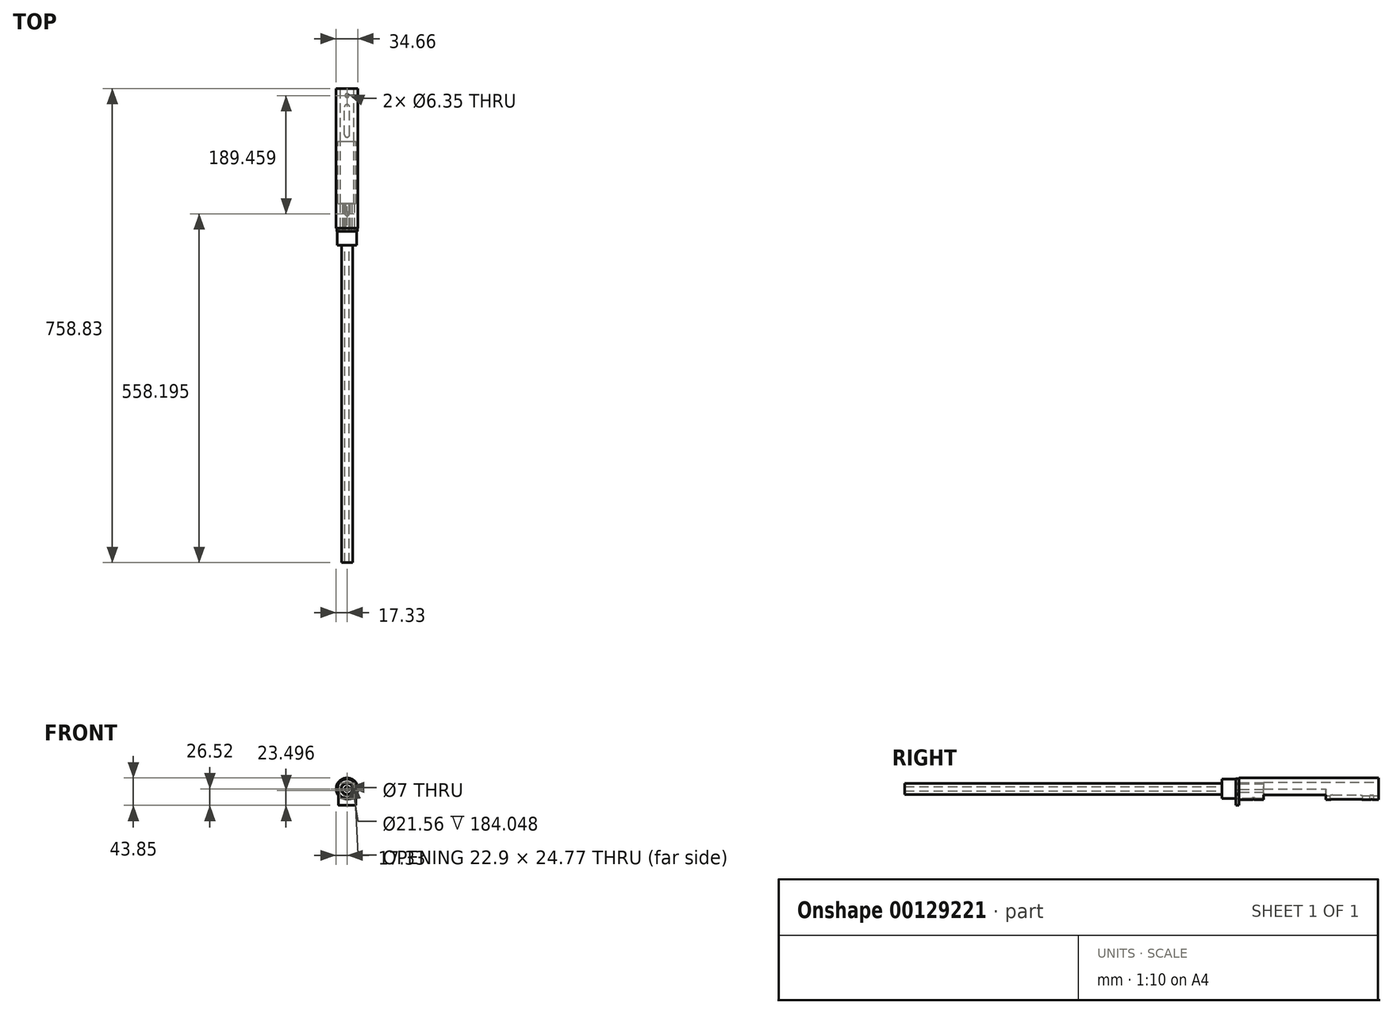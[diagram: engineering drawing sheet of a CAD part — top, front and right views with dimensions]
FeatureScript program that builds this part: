
annotation { "Feature Type Name" : "Feature", "Feature Type Description" : "" }
export const myFeature = defineFeature(function(context is Context, id is Id, definition is map)
    precondition{}
    {
        {
            var Q0;
            Q0=qCreatedBy(makeId("Front.planeOp"),FACE);
            var sketch = newSketch(context, id + "F0", { "sketchPlane" : qUnion([Q0])});
            skCircle(sketch, "E0", {"center": v(0, 0) * mm, "radius": 17.33 * mm});
            skCircle(sketch, "E1.0", {"center": v(0, 0) * mm, "radius": 10.78 * mm});
            skSolve(sketch);
        }
        {
            var Q0;
            Q0 = qSketchRegion(id + "F0", true);
            extrude(context, id + "F1", {"entities" : qUnion([Q0]), "depth" : 184.05 * mm, "offsetDistance" : 25.4 * mm});
        }
        {
            var Q0;
            Q0=makeQuery(id+"F1.opExtrude","CAP_FACE",FACE,{"disambiguationData":[OSD([sQuery(id+"F0.wireOp",EDGE,"E0"),sQuery(id+"F0.wireOp",EDGE,"E1.0")])],"isStart":false});
            var sketch = newSketch(context, id + "F2", { "sketchPlane" : qUnion([Q0])});
            skCircle(sketch, "E2.0", {"center": v(0, 0) * mm, "radius": 17.33 * mm});
            skSolve(sketch);
        }
        {
            var Q0;
            Q0 = qSketchRegion(id + "F2", true);
            extrude(context, id + "F3", {"entities" : qUnion([Q0]), "operationType" : NewBodyOperationType.ADD, "depth" : 39.5 * mm, "offsetDistance" : 25.4 * mm});
        }
        {
            var Q0;
            Q0=makeQuery(id+"F3.opExtrude","CAP_FACE",FACE,{"disambiguationData":[OSD([sQuery(id+"F2.wireOp",EDGE,"E2.0")])],"isStart":false});
            var sketch = newSketch(context, id + "F4", { "sketchPlane" : qUnion([Q0])});
            skArc(sketch, "E3", {"start": v(2.66, 7.14) * mm, "mid": v(0, 7.62) * mm, "end": v(-2.66, 7.14) * mm});
            skLineSegment(sketch, "E4", {"start": v(2.66, 7.14) * mm, "end": v(6.43, 9.32) * mm});
            skLineSegment(sketch, "E5", {"start": v(6.87, 9.2) * mm, "end": v(11.4, 1.35) * mm});
            skLineSegment(sketch, "E6", {"start": v(11.29, 0.9) * mm, "end": v(7.51, -1.27) * mm});
            skLineSegment(sketch, "E7.1.0", {"start": v(-6.43, 9.32) * mm, "end": v(-2.66, 7.14) * mm});
            skLineSegment(sketch, "E7.1.1", {"start": v(-11.4, 1.35) * mm, "end": v(-6.87, 9.2) * mm});
            skLineSegment(sketch, "E7.1.2", {"start": v(-7.51, -1.27) * mm, "end": v(-11.29, 0.9) * mm});
            skLineSegment(sketch, "E7.2.0", {"start": v(-4.86, -10.55) * mm, "end": v(-4.86, -5.87) * mm});
            skLineSegment(sketch, "E7.2.1", {"start": v(4.86, -10.55) * mm, "end": v(-4.86, -10.55) * mm, "construction": true});
            skLineSegment(sketch, "E7.2.2", {"start": v(4.86, -5.87) * mm, "end": v(4.86, -10.55) * mm});
            skPoint(sketch, "E8", {"position": v(0, -10.55) * mm});
            skArc(sketch, "E9", {"start": v(-4.86, -10.55) * mm, "mid": v(0, -15.41) * mm, "end": v(4.86, -10.55) * mm});
            skArc(sketch, "E10.trimOffspring", {"start": v(4.86, -5.87) * mm, "mid": v(6.6, -3.8) * mm, "end": v(7.51, -1.27) * mm});
            skArc(sketch, "E11.trimOffspring", {"start": v(-7.51, -1.27) * mm, "mid": v(-6.6, -3.8) * mm, "end": v(-4.86, -5.87) * mm});
            skPoint(sketch, "E12.visualSharp", {"position": v(11.57, 1.07) * mm});
            skArc(sketch, "E12.filletArc", {"start": v(11.29, 0.9) * mm, "mid": v(11.44, 1.1) * mm, "end": v(11.4, 1.35) * mm});
            skPoint(sketch, "E13.visualSharp", {"position": v(6.71, 9.48) * mm});
            skArc(sketch, "E13.filletArc", {"start": v(6.87, 9.2) * mm, "mid": v(6.68, 9.35) * mm, "end": v(6.43, 9.32) * mm});
            skPoint(sketch, "E14.visualSharp", {"position": v(-6.71, 9.48) * mm});
            skArc(sketch, "E14.filletArc", {"start": v(-6.43, 9.32) * mm, "mid": v(-6.68, 9.35) * mm, "end": v(-6.87, 9.2) * mm});
            skPoint(sketch, "E15.visualSharp", {"position": v(-11.57, 1.07) * mm});
            skArc(sketch, "E15.filletArc", {"start": v(-11.4, 1.35) * mm, "mid": v(-11.44, 1.1) * mm, "end": v(-11.29, 0.9) * mm});
            skSolve(sketch);
        }
        {
            var Q0;
            Q0 = qSketchRegion(id + "F4", true);
            var Q1;
            Q1=makeQuery(id+"F3.opExtrude","CAP_FACE",FACE,{"disambiguationData":[OSD([sQuery(id+"F2.wireOp",EDGE,"E2.0")])],"isStart":true});
            extrude(context, id + "F5", {"entities" : qUnion([Q0]), "operationType" : NewBodyOperationType.REMOVE, "endBound" : BoundingType.UP_TO_SURFACE, "oppositeDirection" : true, "depth" : 25.4 * mm, "endBoundEntityFace" : qUnion([Q1]), "offsetDistance" : 25.4 * mm});
        }
        {
            var Q0;
            Q0=makeQuery(id+"F3.opExtrude","CAP_FACE",FACE,{"disambiguationData":[OSD([sQuery(id+"F2.wireOp",EDGE,"E2.0")])],"isStart":false});
            var sketch = newSketch(context, id + "F6", { "sketchPlane" : qUnion([Q0])});
            skArc(sketch, "E16", {"start": v(13.92, -8.94) * mm, "mid": v(0, 16.54) * mm, "end": v(-13.92, -8.94) * mm});
            skLineSegment(sketch, "E17", {"start": v(-13.92, -8.94) * mm, "end": v(-13.92, -25.74) * mm});
            skLineSegment(sketch, "E18", {"start": v(-13.13, -26.52) * mm, "end": v(13.13, -26.52) * mm});
            skLineSegment(sketch, "E19", {"start": v(13.92, -25.74) * mm, "end": v(13.92, -8.94) * mm});
            skPoint(sketch, "E20", {"position": v(0, -26.52) * mm});
            skPoint(sketch, "E21.visualSharp", {"position": v(-13.92, -26.52) * mm});
            skArc(sketch, "E21.filletArc", {"start": v(-13.92, -25.74) * mm, "mid": v(-13.69, -26.3) * mm, "end": v(-13.13, -26.52) * mm});
            skPoint(sketch, "E22.visualSharp", {"position": v(13.92, -26.52) * mm});
            skArc(sketch, "E22.filletArc", {"start": v(13.13, -26.52) * mm, "mid": v(13.69, -26.3) * mm, "end": v(13.92, -25.74) * mm});
            skArc(sketch, "E23", {"start": v(-7.51, -1.27) * mm, "mid": v(-6.6, -3.8) * mm, "end": v(-4.86, -5.87) * mm});
            skLineSegment(sketch, "E24", {"start": v(-7.51, -1.27) * mm, "end": v(-11.29, 0.9) * mm});
            skArc(sketch, "E25", {"start": v(-11.4, 1.35) * mm, "mid": v(-11.44, 1.1) * mm, "end": v(-11.29, 0.9) * mm});
            skLineSegment(sketch, "E26", {"start": v(-11.4, 1.35) * mm, "end": v(-6.87, 9.2) * mm});
            skArc(sketch, "E27", {"start": v(-6.43, 9.32) * mm, "mid": v(-6.68, 9.35) * mm, "end": v(-6.87, 9.2) * mm});
            skLineSegment(sketch, "E28", {"start": v(-6.43, 9.32) * mm, "end": v(-2.66, 7.14) * mm});
            skArc(sketch, "E29", {"start": v(2.66, 7.14) * mm, "mid": v(0, 7.62) * mm, "end": v(-2.66, 7.14) * mm});
            skLineSegment(sketch, "E30", {"start": v(2.66, 7.14) * mm, "end": v(6.43, 9.32) * mm});
            skArc(sketch, "E31", {"start": v(6.87, 9.2) * mm, "mid": v(6.68, 9.35) * mm, "end": v(6.43, 9.32) * mm});
            skLineSegment(sketch, "E32", {"start": v(6.87, 9.2) * mm, "end": v(11.4, 1.35) * mm});
            skArc(sketch, "E33", {"start": v(11.29, 0.9) * mm, "mid": v(11.44, 1.1) * mm, "end": v(11.4, 1.35) * mm});
            skLineSegment(sketch, "E34", {"start": v(11.29, 0.9) * mm, "end": v(7.51, -1.27) * mm});
            skArc(sketch, "E35", {"start": v(4.86, -5.87) * mm, "mid": v(6.6, -3.8) * mm, "end": v(7.51, -1.27) * mm});
            skLineSegment(sketch, "E36", {"start": v(4.86, -5.87) * mm, "end": v(4.86, -10.55) * mm});
            skArc(sketch, "E37", {"start": v(-4.86, -10.55) * mm, "mid": v(0, -15.41) * mm, "end": v(4.86, -10.55) * mm});
            skLineSegment(sketch, "E38", {"start": v(-4.86, -10.55) * mm, "end": v(-4.86, -5.87) * mm});
            skSolve(sketch);
        }
        {
            var Q0;
            Q0 = qSketchRegion(id + "F6", true);
            extrude(context, id + "F7", {"entities" : qUnion([Q0]), "depth" : 4.97 * mm, "offsetDistance" : 25.4 * mm});
        }
        {
            var Q0;
            Q0=makeQuery(id+"F7.opExtrude","CAP_FACE",FACE,{"disambiguationData":[OSD([sQuery(id+"F6.wireOp",EDGE,"E16"),sQuery(id+"F6.wireOp",EDGE,"E17"),sQuery(id+"F6.wireOp",EDGE,"E18"),sQuery(id+"F6.wireOp",EDGE,"E19"),sQuery(id+"F6.wireOp",EDGE,"E21.filletArc"),sQuery(id+"F6.wireOp",EDGE,"E22.filletArc"),sQuery(id+"F6.wireOp",EDGE,"E23"),sQuery(id+"F6.wireOp",EDGE,"E24"),sQuery(id+"F6.wireOp",EDGE,"E25"),sQuery(id+"F6.wireOp",EDGE,"E26"),sQuery(id+"F6.wireOp",EDGE,"E27"),sQuery(id+"F6.wireOp",EDGE,"E28"),sQuery(id+"F6.wireOp",EDGE,"E29"),sQuery(id+"F6.wireOp",EDGE,"E30"),sQuery(id+"F6.wireOp",EDGE,"E31"),sQuery(id+"F6.wireOp",EDGE,"E32"),sQuery(id+"F6.wireOp",EDGE,"E33"),sQuery(id+"F6.wireOp",EDGE,"E34"),sQuery(id+"F6.wireOp",EDGE,"E35"),sQuery(id+"F6.wireOp",EDGE,"E36"),sQuery(id+"F6.wireOp",EDGE,"E37"),sQuery(id+"F6.wireOp",EDGE,"E38")])],"isStart":false});
            var sketch = newSketch(context, id + "F8", { "sketchPlane" : qUnion([Q0])});
            skCircle(sketch, "E39", {"center": v(0, 0) * mm, "radius": 15.41 * mm});
            skSolve(sketch);
        }
        {
            var Q0;
            Q0 = qSketchRegion(id + "F8", true);
            extrude(context, id + "F9", {"entities" : qUnion([Q0]), "depth" : 22.3 * mm, "offsetDistance" : 25.4 * mm});
        }
        {
            var Q0;
            Q0=makeQuery(id+"F9.opExtrude","CAP_FACE",FACE,{"disambiguationData":[OSD([sQuery(id+"F8.wireOp",EDGE,"E39")])],"isStart":false});
            var sketch = newSketch(context, id + "F10", { "sketchPlane" : qUnion([Q0])});
            skCircle(sketch, "E40", {"center": v(0, 0) * mm, "radius": 8.9 * mm});
            skCircle(sketch, "E41", {"center": v(0, 0) * mm, "radius": 3.5 * mm});
            skSolve(sketch);
        }
        {
            var Q0;
            Q0=makeQuery(id+"F10.imprint","IMPRINT",FACE,{"disambiguationData":[TD([[makeQuery(id+"F10.imprint","IMPRINT",EDGE,{"derivedFrom":sQuery(id+"F10.wireOp",EDGE,"E40")}),1.0]])]});
            var Q1;
            Q1=sQuery(id+"F10.wireOp",EDGE,"E40");
            extrude(context, id + "F11", {"entities" : qUnion([Q0]), "surfaceEntities" : qUnion([Q1]), "depth" : 508 * mm, "offsetDistance" : 25.4 * mm});
        }
        {
            var Q0;
            Q0=qCreatedBy(makeId("Top.planeOp"),FACE);
            var sketch = newSketch(context, id + "F12", { "sketchPlane" : qUnion([Q0])});
            skLineSegment(sketch, "E42.bottom", {"start": v(-14.26, -184.12) * mm, "end": v(14.26, -184.12) * mm});
            skLineSegment(sketch, "E42.top", {"start": v(-14.26, -84.7) * mm, "end": v(14.26, -84.7) * mm});
            skLineSegment(sketch, "E42.left", {"start": v(-14.26, -184.12) * mm, "end": v(-14.26, -84.7) * mm});
            skLineSegment(sketch, "E42.right", {"start": v(14.26, -184.12) * mm, "end": v(14.26, -84.7) * mm});
            skPoint(sketch, "E43", {"position": v(0, -84.7) * mm});
            skSolve(sketch);
        }
        {
            var Q0;
            Q0 = qSketchRegion(id + "F12", true);
            extrude(context, id + "F13", {"entities" : qUnion([Q0]), "operationType" : NewBodyOperationType.REMOVE, "oppositeDirection" : true, "depth" : 25.4 * mm, "offsetDistance" : 25.4 * mm});
        }
        {
            var Q0;
            Q0=qCreatedBy(makeId("Top.planeOp"),FACE);
            var sketch = newSketch(context, id + "F14", { "sketchPlane" : qUnion([Q0])});
            skLineSegment(sketch, "E44", {"start": v(0, -29.51) * mm, "end": v(0, -73.77) * mm, "construction": true});
            skArc(sketch, "E45.0.startCap", {"start": v(-4.06, -29.51) * mm, "mid": v(0, -25.45) * mm, "end": v(4.06, -29.51) * mm});
            skArc(sketch, "E45.0.endCap", {"start": v(4.06, -73.77) * mm, "mid": v(0, -77.84) * mm, "end": v(-4.06, -73.77) * mm});
            skLineSegment(sketch, "E45.0.left", {"start": v(4.06, -29.51) * mm, "end": v(4.06, -73.77) * mm});
            skLineSegment(sketch, "E45.0.right", {"start": v(-4.06, -29.51) * mm, "end": v(-4.06, -73.77) * mm});
            skCircle(sketch, "E46", {"center": v(0, -11.18) * mm, "radius": 3.18 * mm});
            skCircle(sketch, "E47", {"center": v(0, -200.63) * mm, "radius": 3.18 * mm});
            skSolve(sketch);
        }
        {
            var Q0;
            Q0 = qSketchRegion(id + "F14", true);
            extrude(context, id + "F15", {"entities" : qUnion([Q0]), "operationType" : NewBodyOperationType.REMOVE, "oppositeDirection" : true, "depth" : 25.4 * mm, "offsetDistance" : 25.4 * mm});
        }
    });
